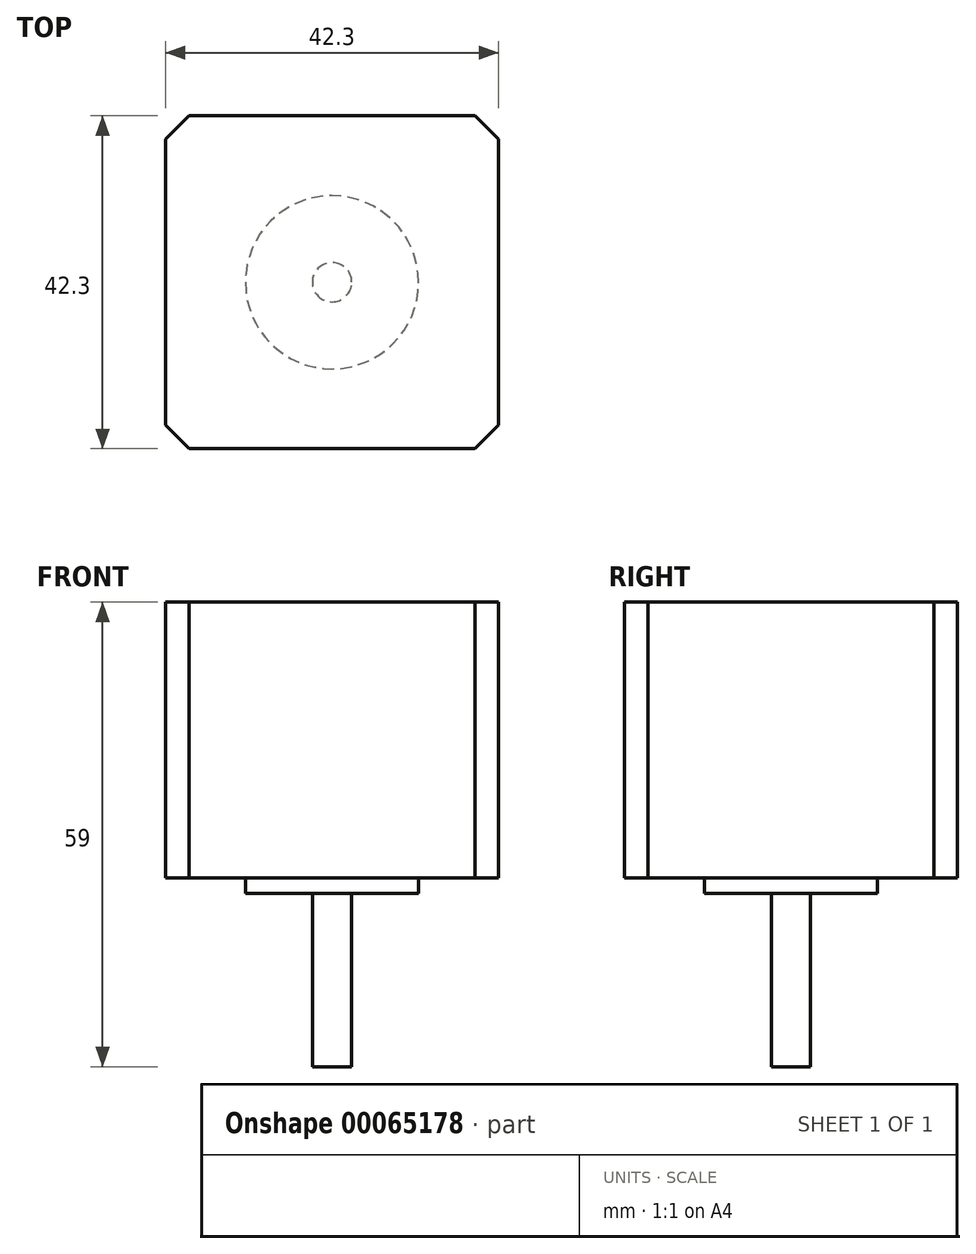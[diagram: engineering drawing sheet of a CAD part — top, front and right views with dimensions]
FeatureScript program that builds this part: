
annotation { "Feature Type Name" : "Feature", "Feature Type Description" : "" }
export const myFeature = defineFeature(function(context is Context, id is Id, definition is map)
    precondition{}
    {
        {
            var Q0;
            Q0=qCreatedBy(makeId("Top.planeOp"),FACE);
            var sketch = newSketch(context, id + "F0", { "sketchPlane" : qUnion([Q0])});
            skLineSegment(sketch, "E0.bottom", {"start": v(21.15, 21.15) * mm, "end": v(-21.15, 21.15) * mm});
            skLineSegment(sketch, "E0.top", {"start": v(21.15, -21.15) * mm, "end": v(-21.15, -21.15) * mm});
            skLineSegment(sketch, "E0.left", {"start": v(21.15, 21.15) * mm, "end": v(21.15, -21.15) * mm});
            skLineSegment(sketch, "E0.right", {"start": v(-21.15, 21.15) * mm, "end": v(-21.15, -21.15) * mm});
            skPoint(sketch, "E0.middle", {"position": v(0, 0) * mm});
            skCircle(sketch, "E1", {"center": v(0, 0) * mm, "radius": 11 * mm});
            skCircle(sketch, "E2", {"center": v(0, 0) * mm, "radius": 2.5 * mm});
            skSolve(sketch);
        }
        {
            var Q0;
            Q0=makeQuery(id+"F0.imprint","IMPRINT",FACE,{"disambiguationData":[TD([[makeQuery(id+"F0.imprint","IMPRINT",EDGE,{"derivedFrom":sQuery(id+"F0.wireOp",EDGE,"E0.bottom")}),1.0]])]});
            var Q1;
            Q1=makeQuery(id+"F0.imprint","IMPRINT",FACE,{"disambiguationData":[TD([[makeQuery(id+"F0.imprint","IMPRINT",EDGE,{"derivedFrom":sQuery(id+"F0.wireOp",EDGE,"E2")}),1.0]])]});
            var Q2;
            Q2=makeQuery(id+"F0.imprint","IMPRINT",FACE,{"disambiguationData":[TD([[makeQuery(id+"F0.imprint","IMPRINT",EDGE,{"derivedFrom":sQuery(id+"F0.wireOp",EDGE,"E1")}),1.0]])]});
            extrude(context, id + "F1", {"entities" : qUnion([Q0, Q1, Q2]), "depth" : 35 * mm});
        }
        {
            var Q0;
            Q0=makeQuery(id+"F0.imprint","IMPRINT",FACE,{"disambiguationData":[TD([[makeQuery(id+"F0.imprint","IMPRINT",EDGE,{"derivedFrom":sQuery(id+"F0.wireOp",EDGE,"E2")}),1.0]])]});
            extrude(context, id + "F2", {"entities" : qUnion([Q0]), "operationType" : NewBodyOperationType.ADD, "oppositeDirection" : true, "depth" : 24 * mm});
        }
        {
            var Q0;
            Q0=makeQuery(id+"F0.imprint","IMPRINT",FACE,{"disambiguationData":[TD([[makeQuery(id+"F0.imprint","IMPRINT",EDGE,{"derivedFrom":sQuery(id+"F0.wireOp",EDGE,"E1")}),1.0]])]});
            extrude(context, id + "F3", {"entities" : qUnion([Q0]), "operationType" : NewBodyOperationType.ADD, "oppositeDirection" : true, "depth" : 2 * mm});
        }
        {
            var Q0;
            Q0=makeQuery(id+"F1.opExtrude","SWEPT_EDGE",EDGE,{"disambiguationData":[OSD([sQuery(id+"F0.wireOp",EDGE,"E0.top"),sQuery(id+"F0.wireOp",EDGE,"E0.right")])]});
            var Q1;
            Q1=makeQuery(id+"F1.opExtrude","SWEPT_EDGE",EDGE,{"disambiguationData":[OSD([sQuery(id+"F0.wireOp",EDGE,"E0.top"),sQuery(id+"F0.wireOp",EDGE,"E0.left")])]});
            var Q2;
            Q2=makeQuery(id+"F1.opExtrude","SWEPT_EDGE",EDGE,{"disambiguationData":[OSD([sQuery(id+"F0.wireOp",EDGE,"E0.bottom"),sQuery(id+"F0.wireOp",EDGE,"E0.left")])]});
            var Q3;
            Q3=makeQuery(id+"F1.opExtrude","SWEPT_EDGE",EDGE,{"disambiguationData":[OSD([sQuery(id+"F0.wireOp",EDGE,"E0.bottom"),sQuery(id+"F0.wireOp",EDGE,"E0.right")])]});
            chamfer(context, id + "F4", {"entities" : qUnion([Q0, Q1, Q2, Q3]), "width" : 3 * mm, "tangentPropagation" : true});
        }
    });
